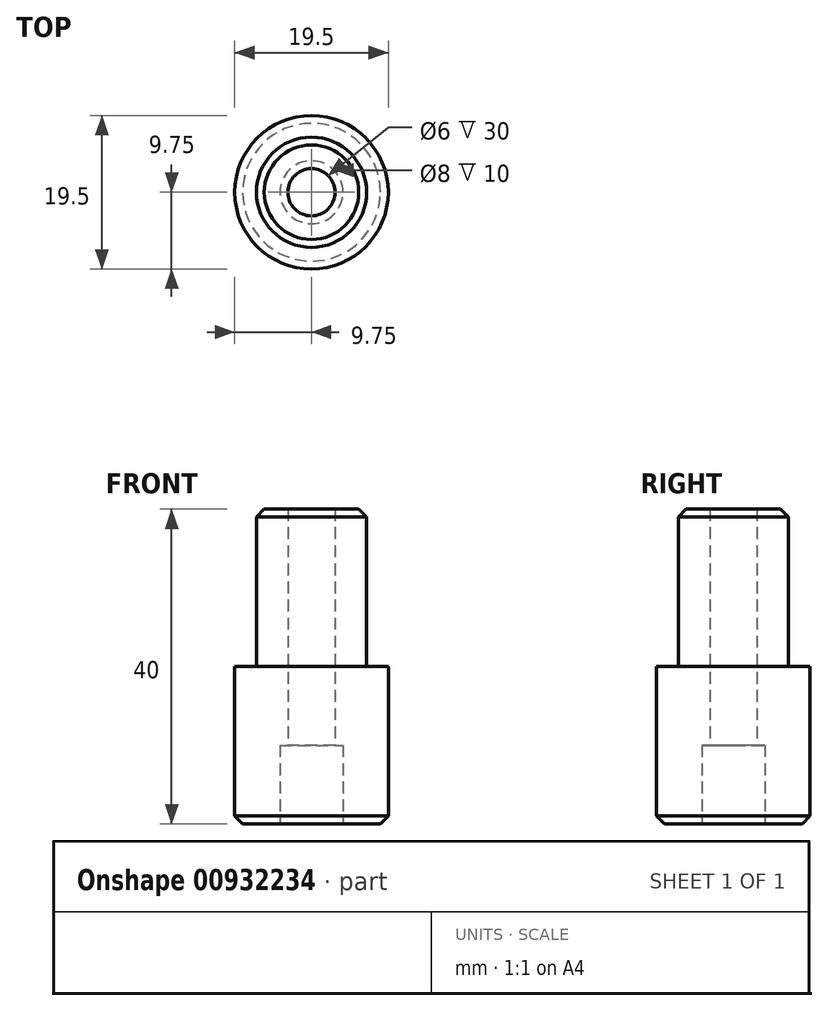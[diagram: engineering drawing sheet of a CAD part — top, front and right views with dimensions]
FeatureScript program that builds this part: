
annotation { "Feature Type Name" : "Feature", "Feature Type Description" : "" }
export const myFeature = defineFeature(function(context is Context, id is Id, definition is map)
    precondition{}
    {
        {
            var Q0;
            Q0=qCreatedBy(makeId("Top.planeOp"),FACE);
            var sketch = newSketch(context, id + "F0", { "sketchPlane" : qUnion([Q0])});
            skCircle(sketch, "E0", {"center": v(0, 0) * mm, "radius": 9.75 * mm});
            skCircle(sketch, "E1", {"center": v(0, 0) * mm, "radius": 7 * mm});
            skCircle(sketch, "E2", {"center": v(0, 0) * mm, "radius": 3 * mm});
            skSolve(sketch);
        }
        {
            var Q0;
            Q0=makeQuery(id+"F0.imprint","IMPRINT",FACE,{"disambiguationData":[TD([[makeQuery(id+"F0.imprint","IMPRINT",EDGE,{"derivedFrom":sQuery(id+"F0.wireOp",EDGE,"E1")}),1.0]])]});
            extrude(context, id + "F1", {"entities" : qUnion([Q0]), "depth" : 20 * mm, "offsetDistance" : 25 * mm});
        }
        {
            var Q0;
            Q0=makeQuery(id+"F0.imprint","IMPRINT",FACE,{"disambiguationData":[TD([[makeQuery(id+"F0.imprint","IMPRINT",EDGE,{"derivedFrom":sQuery(id+"F0.wireOp",EDGE,"E0")}),1.0]])]});
            var Q1;
            Q1=makeQuery(id+"F0.imprint","IMPRINT",FACE,{"disambiguationData":[TD([[makeQuery(id+"F0.imprint","IMPRINT",EDGE,{"derivedFrom":sQuery(id+"F0.wireOp",EDGE,"E1")}),1.0]])]});
            extrude(context, id + "F2", {"entities" : qUnion([Q0, Q1]), "operationType" : NewBodyOperationType.ADD, "oppositeDirection" : true, "depth" : 20 * mm, "offsetDistance" : 25 * mm});
        }
        {
            var Q0;
            Q0=makeQuery(id+"F2.opExtrude","CAP_FACE",FACE,{"disambiguationData":[OSD([sQuery(id+"F0.wireOp",EDGE,"E0"),sQuery(id+"F0.wireOp",EDGE,"E2")])],"isStart":false});
            var sketch = newSketch(context, id + "F3", { "sketchPlane" : qUnion([Q0])});
            skCircle(sketch, "E3", {"center": v(0, 0) * mm, "radius": 4 * mm});
            skSolve(sketch);
        }
        {
            var Q0;
            Q0=makeQuery(id+"F3.imprint","IMPRINT",FACE,{"disambiguationData":[TD([[makeQuery(id+"F3.imprint","IMPRINT",EDGE,{"derivedFrom":sQuery(id+"F3.wireOp",EDGE,"E3")}),1.0]])]});
            extrude(context, id + "F4", {"entities" : qUnion([Q0]), "operationType" : NewBodyOperationType.REMOVE, "oppositeDirection" : true, "depth" : 10 * mm, "offsetDistance" : 25 * mm});
        }
        {
            var Q0;
            Q0=makeQuery(id+"F2.opExtrude","CAP_EDGE",EDGE,{"disambiguationData":[OSD([sQuery(id+"F0.wireOp",EDGE,"E0")])],"isStart":false});
            var Q1;
            Q1=makeQuery(id+"F1.opExtrude","CAP_EDGE",EDGE,{"disambiguationData":[OSD([sQuery(id+"F0.wireOp",EDGE,"E1")])],"isStart":false});
            var Q2;
            Q2=makeQuery(id+"F4.boolean.opBoolean","COPY",EDGE,{"derivedFrom":makeQuery(id+"F4.opExtrude","CAP_EDGE",EDGE,{"disambiguationData":[OSD([sQuery(id+"F0.wireOp",EDGE,"E2")])],"isStart":false})});
            chamfer(context, id + "F5", {"entities" : qUnion([Q0, Q1, Q2]), "width" : 1 * mm, "tangentPropagation" : true});
        }
    });
